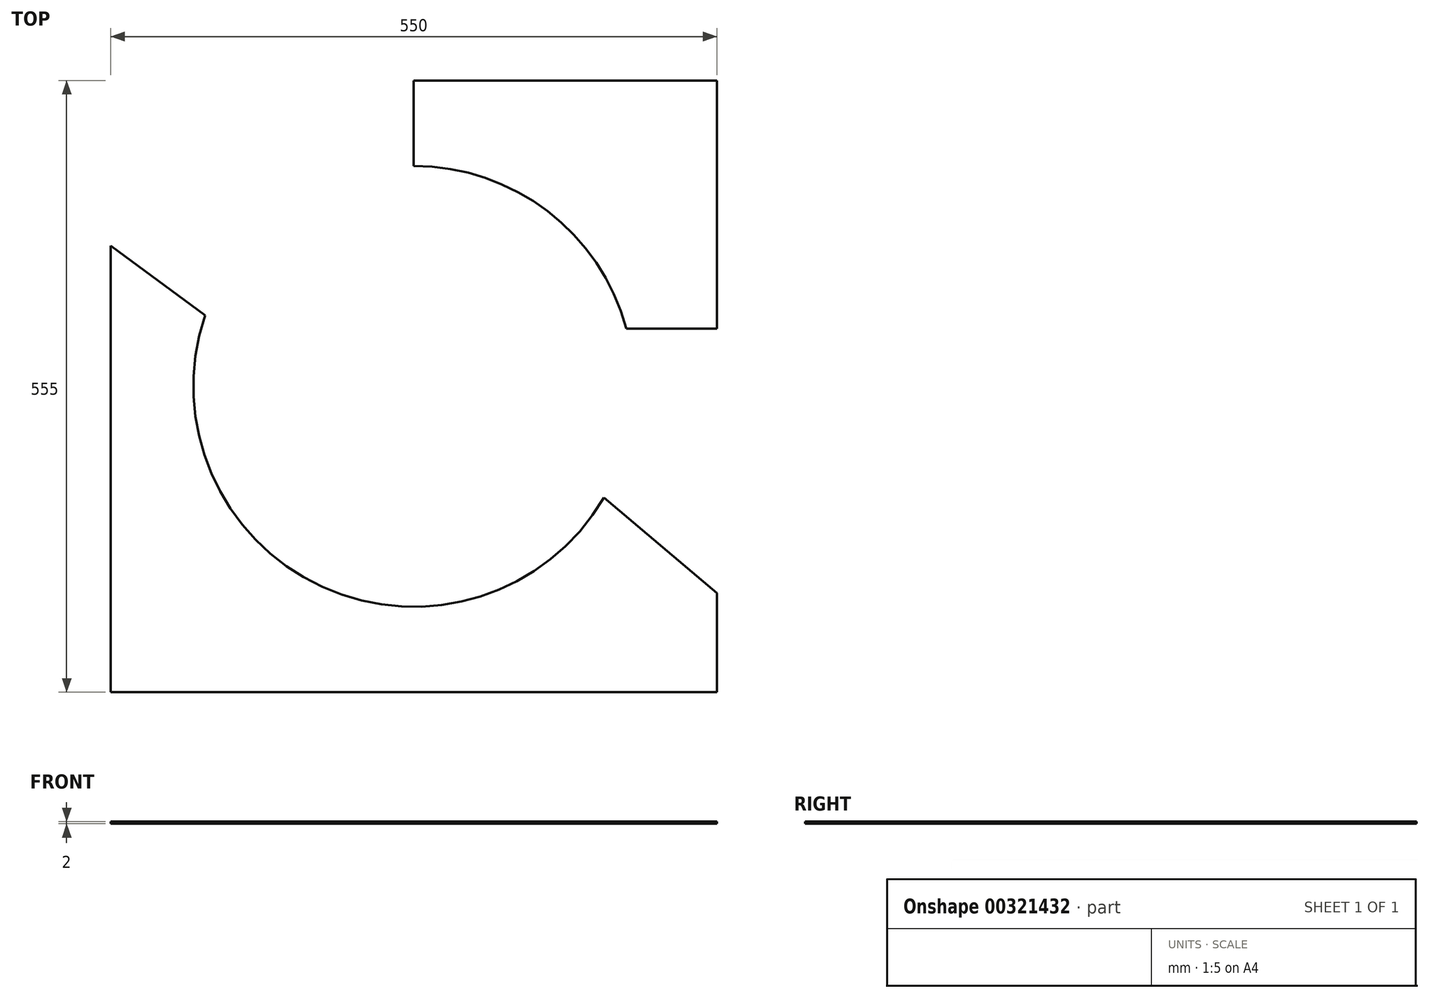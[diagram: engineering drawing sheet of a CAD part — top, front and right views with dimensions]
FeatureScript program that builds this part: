
annotation { "Feature Type Name" : "Feature", "Feature Type Description" : "" }
export const myFeature = defineFeature(function(context is Context, id is Id, definition is map)
    precondition{}
    {
        {
            var Q0;
            Q0=qCreatedBy(makeId("Top.planeOp"),FACE);
            var sketch = newSketch(context, id + "F0", { "sketchPlane" : qUnion([Q0])});
            skLineSegment(sketch, "E0.bottom", {"start": v(-275, 277.5) * mm, "end": v(0, 277.5) * mm, "construction": true});
            skLineSegment(sketch, "E0.top", {"start": v(-275, -277.5) * mm, "end": v(275, -277.5) * mm});
            skLineSegment(sketch, "E0.left", {"start": v(-275, 277.5) * mm, "end": v(-275, 127.5) * mm, "construction": true});
            skLineSegment(sketch, "E0.right", {"start": v(275, 277.5) * mm, "end": v(275, 52.5) * mm});
            skLineSegment(sketch, "E1", {"start": v(275, -187.5) * mm, "end": v(275, -277.5) * mm});
            skLineSegment(sketch, "E2", {"start": v(-275, 127.5) * mm, "end": v(-275, -277.5) * mm});
            skLineSegment(sketch, "E3", {"start": v(0, 277.5) * mm, "end": v(275, 277.5) * mm});
            skLineSegment(sketch, "E4", {"start": v(275, 52.5) * mm, "end": v(275, -187.5) * mm});
            skLineSegment(sketch, "E5", {"start": v(-275, 277.5) * mm, "end": v(275, -277.5) * mm, "construction": true});
            skLineSegment(sketch, "E6", {"start": v(275, 277.5) * mm, "end": v(-275, -277.5) * mm, "construction": true});
            skLineSegment(sketch, "E7", {"start": v(-275, 277.5) * mm, "end": v(172.65, -100.96) * mm, "construction": true});
            skLineSegment(sketch, "E8", {"start": v(172.65, -100.96) * mm, "end": v(275, -187.5) * mm});
            skLineSegment(sketch, "E9", {"start": v(-275, 127.5) * mm, "end": v(-189.34, 64.42) * mm});
            skLineSegment(sketch, "E10", {"start": v(117.72, -161.68) * mm, "end": v(275, -277.5) * mm, "construction": true});
            skLineSegment(sketch, "E11", {"start": v(-189.34, 64.42) * mm, "end": v(117.72, -161.68) * mm, "construction": true});
            skLineSegment(sketch, "E12", {"start": v(0, 277.5) * mm, "end": v(0, 200) * mm});
            skArc(sketch, "E13", {"start": v(0, 200) * mm, "mid": v(-116.44, 162.61) * mm, "end": v(-189.34, 64.42) * mm, "construction": true});
            skArc(sketch, "E14", {"start": v(-189.34, 64.42) * mm, "mid": v(-118.59, -161.05) * mm, "end": v(117.72, -161.68) * mm});
            skArc(sketch, "E15", {"start": v(192.99, 52.5) * mm, "mid": v(121.45, 158.9) * mm, "end": v(0, 200) * mm});
            skArc(sketch, "E16", {"start": v(117.72, -161.68) * mm, "mid": v(148.32, -134.16) * mm, "end": v(172.65, -100.96) * mm});
            skLineSegment(sketch, "E17", {"start": v(275, 52.5) * mm, "end": v(192.99, 52.5) * mm});
            skSolve(sketch);
        }
        {
            var Q0;
            Q0 = qSketchRegion(id + "F0", true);
            extrude(context, id + "F1", {"entities" : qUnion([Q0]), "depth" : 2 * mm});
        }
    });
